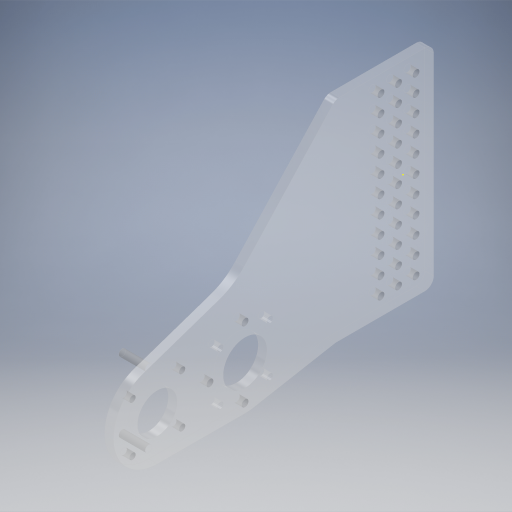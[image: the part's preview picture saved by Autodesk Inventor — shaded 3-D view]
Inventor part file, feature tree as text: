
AUTODESK INVENTOR PART (.ipt)
format: ipt  version: 2024.2 (Build 282272000, 272)  size: 648,192 bytes
history: native  units: in
note: dims shown in document units (in); Inventor stores cm internally (conversion verified against a paired STEP export)
features: sketch x9, extrude x8, projected_geometry x6, other x1
ambient origin geometry x8: Origin, YZ Plane, XZ Plane, XY Plane, X Axis, Y Axis, Z Axis, Center Point
bodies: Solid1 (feature_tree)
feature tree (24):
  extrude  "Extrusion1"  Depth=1.0in
  extrude  "Extrusion2"  Depth=0.707in
  extrude  "Extrusion3"  Depth=0.177in
  extrude  "Extrusion4"  Depth=0.707in
  extrude  "Extrusion5"  Depth=0.707in
  extrude  "Extrusion6"  Depth=0.707in
  sketch  "Sketch8"  dims[d13=0.707in d14=1.0in d15=0.0in]
  extrude  "Extrusion7"  Depth=1.0in TaperAngle=0.0deg
  extrude  "Extrusion8"  Depth=0.196in
  sketch  "Sketch1"  dims[d0=1.0in d1=0.0in d2=0.177in]
  projected_geometry  "Projected Loop1"
  sketch  "Sketch3"  dims[d3=0.707in d4=0.707in]
  projected_geometry  "Projected Loop2"
  sketch  "Sketch4"  dims[d5=0.177in d6=0.177in]
  projected_geometry  "Projected Loop3"
  sketch  "Sketch5"  dims[d7=0.177in d8=0.707in]
  projected_geometry  "Projected Loop4"
  sketch  "Sketch6"  dims[d9=0.707in d10=0.707in]
  projected_geometry  "Projected Loop5"
  sketch  "Sketch7"  dims[d11=0.707in d12=0.707in]
  sketch  "Sketch9"  dims[d16=1.414in d17=0.196in]
  projected_geometry  "Projected Loop6"
  sketch  "Sketch10"  dims[d18=0.0in d19=-1.0in d20=3.1496in d22=360.0deg d24=0.6875in d25=0.0in d26=0.6875in d27=0.0in d28=1.0in d29=0.0in d30=0.196in d31=0.5in d32=0.5in d33=4.3307in d35=0.5in d36=1.1811in d38=0.5in d41=1.0in d42=0.0in d43=1.125in d44=0.177in d45=0.177in d46=0.707in d47=0.707in d48=0.707in d49=0.707in d50=0.707in d51=0.875in d52=0.0in d53=1.0in d54=0.0in d55=0.5in d56=1.9685in]
  other  "Part 2"
